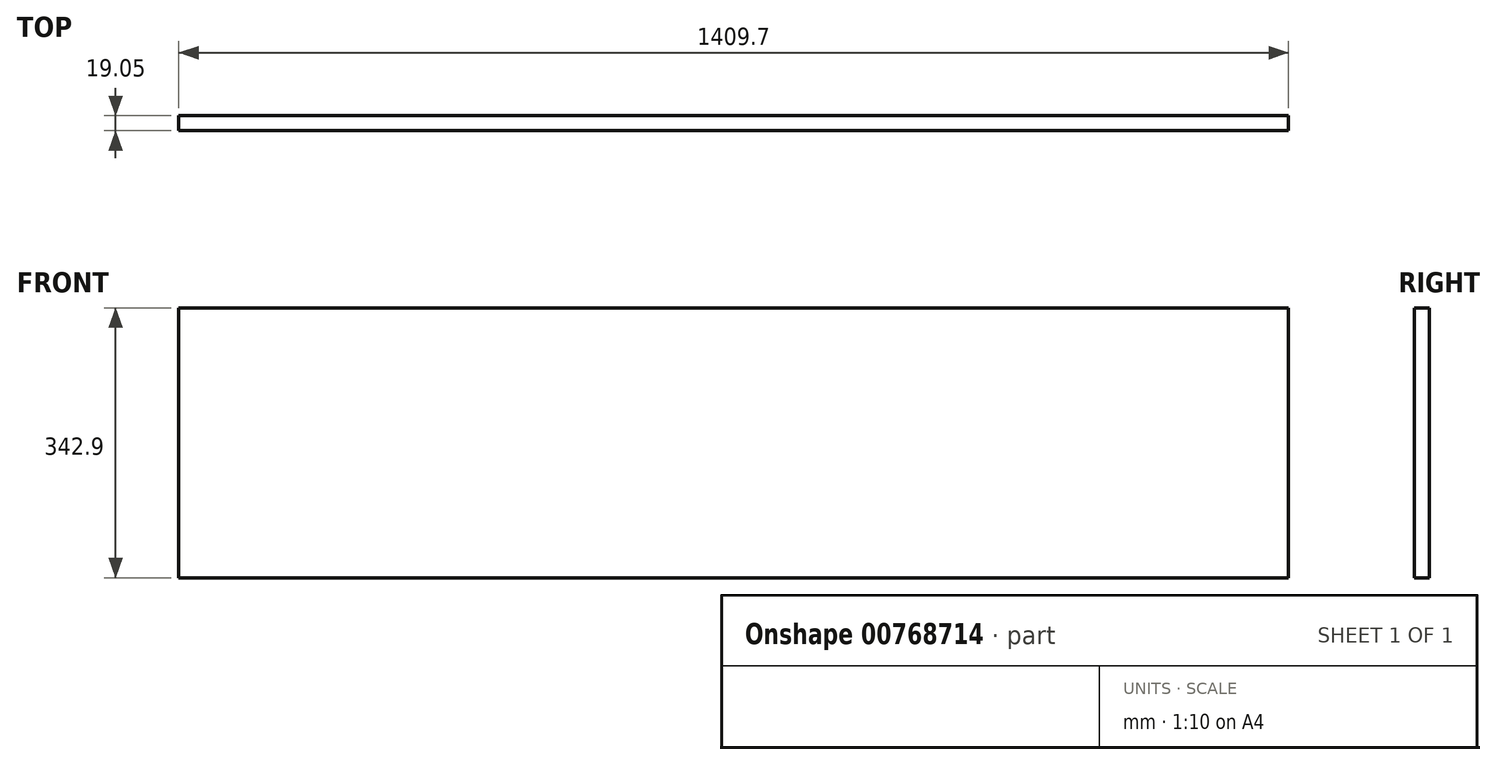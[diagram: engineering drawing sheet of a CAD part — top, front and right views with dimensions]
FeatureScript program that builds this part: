
annotation { "Feature Type Name" : "Feature", "Feature Type Description" : "" }
export const myFeature = defineFeature(function(context is Context, id is Id, definition is map)
    precondition{}
    {
        {
            var Q0;
            Q0=qCreatedBy(makeId("Front.planeOp"),FACE);
            var sketch = newSketch(context, id + "F0", { "sketchPlane" : qUnion([Q0])});
            skLineSegment(sketch, "E0.bottom", {"start": v(-704.85, 171.45) * mm, "end": v(704.85, 171.45) * mm});
            skLineSegment(sketch, "E0.top", {"start": v(-704.85, -171.45) * mm, "end": v(704.85, -171.45) * mm});
            skLineSegment(sketch, "E0.left", {"start": v(-704.85, 171.45) * mm, "end": v(-704.85, -171.45) * mm});
            skLineSegment(sketch, "E0.right", {"start": v(704.85, 171.45) * mm, "end": v(704.85, -171.45) * mm});
            skPoint(sketch, "E0.middle", {"position": v(0, 0) * mm});
            skSolve(sketch);
        }
        {
            var Q0;
            Q0=makeQuery(id+"F0.imprint","IMPRINT",FACE,{"disambiguationData":[TD([[makeQuery(id+"F0.imprint","IMPRINT",EDGE,{"derivedFrom":sQuery(id+"F0.wireOp",EDGE,"E0.bottom")}),-1.0]])]});
            extrude(context, id + "F1", {"entities" : qUnion([Q0]), "depth" : 19.05 * mm, "offsetDistance" : 25.4 * mm});
        }
    });
